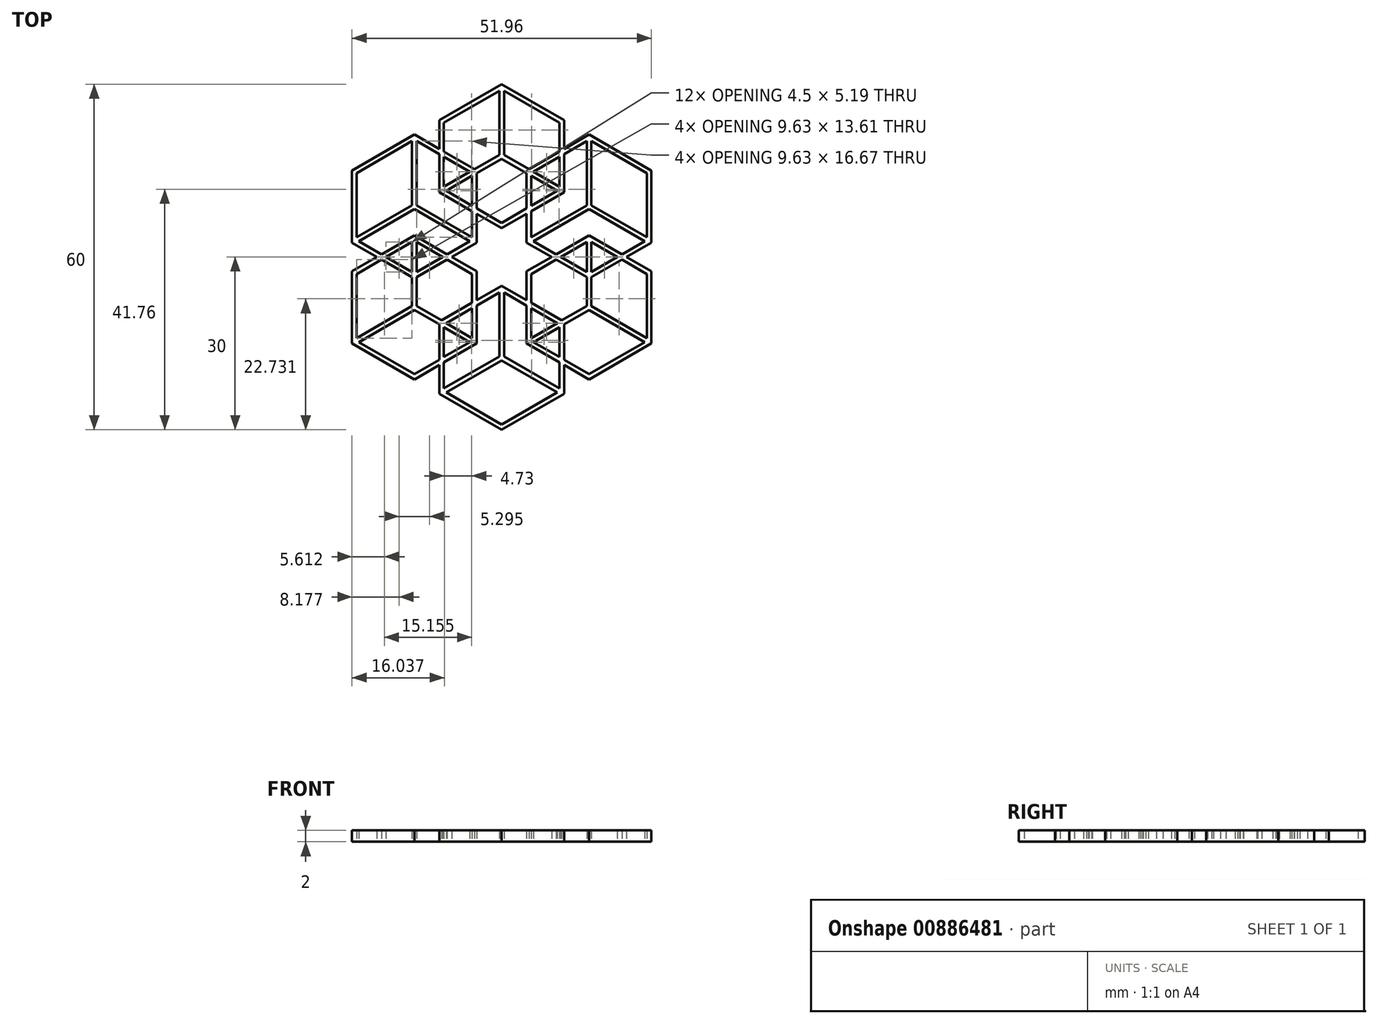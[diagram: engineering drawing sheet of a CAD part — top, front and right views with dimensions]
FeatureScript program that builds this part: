
annotation { "Feature Type Name" : "Feature", "Feature Type Description" : "" }
export const myFeature = defineFeature(function(context is Context, id is Id, definition is map)
    precondition{}
    {
        {
            var Q0;
            Q0=qCreatedBy(makeId("Top.planeOp"),FACE);
            var sketch = newSketch(context, id + "F0", { "sketchPlane" : qUnion([Q0])});
            skCircle(sketch, "E0.cCircle", {"center": v(0, 0) * mm, "radius": 30 * mm, "construction": true});
            skLineSegment(sketch, "E0.0", {"start": v(-25.98, 15) * mm, "end": v(0, 30) * mm, "construction": true});
            skLineSegment(sketch, "E0.1", {"start": v(0, 30) * mm, "end": v(25.98, 15) * mm, "construction": true});
            skLineSegment(sketch, "E0.2", {"start": v(25.98, 15) * mm, "end": v(25.98, -15) * mm, "construction": true});
            skLineSegment(sketch, "E0.3", {"start": v(25.98, -15) * mm, "end": v(0, -30) * mm, "construction": true});
            skLineSegment(sketch, "E0.4", {"start": v(0, -30) * mm, "end": v(-25.98, -15) * mm, "construction": true});
            skLineSegment(sketch, "E0.5", {"start": v(-25.98, -15) * mm, "end": v(-25.98, 15) * mm, "construction": true});
            skCircle(sketch, "E1.cCircle", {"center": v(0, -17.5) * mm, "radius": 12.5 * mm, "construction": true});
            skLineSegment(sketch, "E1.0", {"start": v(0, -30) * mm, "end": v(-10.83, -23.75) * mm});
            skLineSegment(sketch, "E1.1", {"start": v(-10.83, -23.75) * mm, "end": v(-10.83, -11.25) * mm});
            skLineSegment(sketch, "E1.2", {"start": v(-10.83, -11.25) * mm, "end": v(0, -5) * mm});
            skLineSegment(sketch, "E1.3", {"start": v(0, -5) * mm, "end": v(10.83, -11.25) * mm});
            skLineSegment(sketch, "E1.4", {"start": v(10.83, -11.25) * mm, "end": v(10.83, -23.75) * mm});
            skLineSegment(sketch, "E1.5", {"start": v(10.83, -23.75) * mm, "end": v(0, -30) * mm});
            skCircle(sketch, "E2.cCircle", {"center": v(0, -17.5) * mm, "radius": 11.58 * mm, "construction": true});
            skLineSegment(sketch, "E2.0", {"start": v(0.4, -6.15) * mm, "end": v(10.03, -11.71) * mm});
            skLineSegment(sketch, "E2.1", {"start": v(10.03, -11.71) * mm, "end": v(10.03, -22.83) * mm});
            skLineSegment(sketch, "E2.2", {"start": v(9.63, -23.52) * mm, "end": v(0, -29.08) * mm});
            skLineSegment(sketch, "E2.3", {"start": v(0, -29.08) * mm, "end": v(-9.63, -23.52) * mm});
            skLineSegment(sketch, "E2.4", {"start": v(-10.03, -22.83) * mm, "end": v(-10.03, -11.71) * mm});
            skLineSegment(sketch, "E2.5", {"start": v(-10.03, -11.71) * mm, "end": v(-0.4, -6.15) * mm});
            skLineSegment(sketch, "E3.0", {"start": v(0, -17.96) * mm, "end": v(9.63, -23.52) * mm});
            skLineSegment(sketch, "E4.0", {"start": v(0.4, -17.27) * mm, "end": v(10.03, -22.83) * mm});
            skLineSegment(sketch, "E5.0", {"start": v(-0.4, -17.27) * mm, "end": v(-10.03, -22.83) * mm});
            skLineSegment(sketch, "E6.0", {"start": v(0, -17.96) * mm, "end": v(-9.63, -23.52) * mm});
            skPoint(sketch, "E7.orphan", {"position": v(-10.03, -23.29) * mm});
            skLineSegment(sketch, "E8.trimOffspring", {"start": v(-0.4, -6.15) * mm, "end": v(-0.4, -17.27) * mm});
            skLineSegment(sketch, "E9.trimOffspring", {"start": v(0.4, -6.15) * mm, "end": v(0.4, -17.27) * mm});
            skPoint(sketch, "E10.orphan", {"position": v(0, -5.92) * mm});
            skLineSegment(sketch, "E11", {"start": v(0, -17.5) * mm, "end": v(10.83, -23.75) * mm, "construction": true});
            skLineSegment(sketch, "E12", {"start": v(0, -17.5) * mm, "end": v(-10.83, -23.75) * mm, "construction": true});
            skCircle(sketch, "E13.cCircle", {"center": v(15.16, -8.75) * mm, "radius": 12.5 * mm, "construction": true});
            skLineSegment(sketch, "E13.0", {"start": v(15.16, -21.25) * mm, "end": v(4.33, -15) * mm});
            skLineSegment(sketch, "E13.1", {"start": v(4.33, -15) * mm, "end": v(4.33, -2.5) * mm});
            skLineSegment(sketch, "E13.2", {"start": v(4.33, -2.5) * mm, "end": v(15.16, 3.75) * mm});
            skLineSegment(sketch, "E13.3", {"start": v(15.16, 3.75) * mm, "end": v(25.98, -2.5) * mm});
            skLineSegment(sketch, "E13.4", {"start": v(25.98, -2.5) * mm, "end": v(25.98, -15) * mm});
            skLineSegment(sketch, "E13.5", {"start": v(25.98, -15) * mm, "end": v(15.16, -21.25) * mm});
            skCircle(sketch, "E14.cCircle", {"center": v(15.16, -8.75) * mm, "radius": 11.58 * mm, "construction": true});
            skLineSegment(sketch, "E14.0", {"start": v(15.56, 2.6) * mm, "end": v(25.18, -2.96) * mm});
            skLineSegment(sketch, "E14.1", {"start": v(25.18, -2.96) * mm, "end": v(25.18, -14.08) * mm});
            skLineSegment(sketch, "E14.2", {"start": v(24.78, -14.77) * mm, "end": v(15.16, -20.33) * mm});
            skLineSegment(sketch, "E14.3", {"start": v(15.16, -20.33) * mm, "end": v(5.53, -14.77) * mm});
            skLineSegment(sketch, "E14.4", {"start": v(5.13, -14.08) * mm, "end": v(5.13, -2.96) * mm});
            skLineSegment(sketch, "E14.5", {"start": v(5.13, -2.96) * mm, "end": v(14.76, 2.6) * mm});
            skLineSegment(sketch, "E15.0", {"start": v(15.16, -9.21) * mm, "end": v(24.78, -14.77) * mm});
            skLineSegment(sketch, "E16.0", {"start": v(15.56, -8.52) * mm, "end": v(25.18, -14.08) * mm});
            skLineSegment(sketch, "E17.0", {"start": v(14.76, -8.52) * mm, "end": v(5.13, -14.08) * mm});
            skLineSegment(sketch, "E18.0", {"start": v(15.16, -9.21) * mm, "end": v(5.53, -14.77) * mm});
            skPoint(sketch, "E19.orphan", {"position": v(5.13, -14.54) * mm});
            skLineSegment(sketch, "E20.trimOffspring", {"start": v(14.76, 2.6) * mm, "end": v(14.76, -8.52) * mm});
            skLineSegment(sketch, "E21.trimOffspring", {"start": v(15.56, 2.6) * mm, "end": v(15.56, -8.52) * mm});
            skPoint(sketch, "E22.orphan", {"position": v(15.16, 2.83) * mm});
            skLineSegment(sketch, "E23", {"start": v(15.16, -8.75) * mm, "end": v(25.98, -15) * mm, "construction": true});
            skLineSegment(sketch, "E24", {"start": v(15.16, -8.75) * mm, "end": v(4.33, -15) * mm, "construction": true});
            skCircle(sketch, "E25.cCircle", {"center": v(-15.16, -8.75) * mm, "radius": 12.5 * mm, "construction": true});
            skLineSegment(sketch, "E25.0", {"start": v(-15.16, -21.25) * mm, "end": v(-25.98, -15) * mm});
            skLineSegment(sketch, "E25.1", {"start": v(-25.98, -15) * mm, "end": v(-25.98, -2.5) * mm});
            skLineSegment(sketch, "E25.2", {"start": v(-25.98, -2.5) * mm, "end": v(-15.16, 3.75) * mm});
            skLineSegment(sketch, "E25.3", {"start": v(-15.16, 3.75) * mm, "end": v(-4.33, -2.5) * mm});
            skLineSegment(sketch, "E25.4", {"start": v(-4.33, -2.5) * mm, "end": v(-4.33, -15) * mm});
            skLineSegment(sketch, "E25.5", {"start": v(-4.33, -15) * mm, "end": v(-15.16, -21.25) * mm});
            skCircle(sketch, "E26.cCircle", {"center": v(-15.16, -8.75) * mm, "radius": 11.58 * mm, "construction": true});
            skLineSegment(sketch, "E26.0", {"start": v(-14.76, 2.6) * mm, "end": v(-5.13, -2.96) * mm});
            skLineSegment(sketch, "E26.1", {"start": v(-5.13, -2.96) * mm, "end": v(-5.13, -14.08) * mm});
            skLineSegment(sketch, "E26.2", {"start": v(-5.53, -14.77) * mm, "end": v(-15.16, -20.33) * mm});
            skLineSegment(sketch, "E26.3", {"start": v(-15.16, -20.33) * mm, "end": v(-24.78, -14.77) * mm});
            skLineSegment(sketch, "E26.4", {"start": v(-25.18, -14.08) * mm, "end": v(-25.18, -2.96) * mm});
            skLineSegment(sketch, "E26.5", {"start": v(-25.18, -2.96) * mm, "end": v(-15.56, 2.6) * mm});
            skLineSegment(sketch, "E27.0", {"start": v(-15.16, -9.21) * mm, "end": v(-5.53, -14.77) * mm});
            skLineSegment(sketch, "E28.0", {"start": v(-14.76, -8.52) * mm, "end": v(-5.13, -14.08) * mm});
            skLineSegment(sketch, "E29.0", {"start": v(-15.56, -8.52) * mm, "end": v(-25.18, -14.08) * mm});
            skLineSegment(sketch, "E30.0", {"start": v(-15.16, -9.21) * mm, "end": v(-24.78, -14.77) * mm});
            skPoint(sketch, "E31.orphan", {"position": v(-25.18, -14.54) * mm});
            skLineSegment(sketch, "E32.trimOffspring", {"start": v(-15.56, 2.6) * mm, "end": v(-15.56, -8.52) * mm});
            skLineSegment(sketch, "E33.trimOffspring", {"start": v(-14.76, 2.6) * mm, "end": v(-14.76, -8.52) * mm});
            skPoint(sketch, "E34.orphan", {"position": v(-15.16, 2.83) * mm});
            skLineSegment(sketch, "E35", {"start": v(-15.16, -8.75) * mm, "end": v(-4.33, -15) * mm, "construction": true});
            skLineSegment(sketch, "E36", {"start": v(-15.16, -8.75) * mm, "end": v(-25.98, -15) * mm, "construction": true});
            skCircle(sketch, "E37.cCircle", {"center": v(0, 17.5) * mm, "radius": 12.5 * mm, "construction": true});
            skLineSegment(sketch, "E37.0", {"start": v(0, 5) * mm, "end": v(-10.83, 11.25) * mm});
            skLineSegment(sketch, "E37.1", {"start": v(-10.83, 11.25) * mm, "end": v(-10.83, 23.75) * mm});
            skLineSegment(sketch, "E37.2", {"start": v(-10.83, 23.75) * mm, "end": v(0, 30) * mm});
            skLineSegment(sketch, "E37.3", {"start": v(0, 30) * mm, "end": v(10.83, 23.75) * mm});
            skLineSegment(sketch, "E37.4", {"start": v(10.83, 23.75) * mm, "end": v(10.83, 11.25) * mm});
            skLineSegment(sketch, "E37.5", {"start": v(10.83, 11.25) * mm, "end": v(0, 5) * mm});
            skCircle(sketch, "E38.cCircle", {"center": v(0, 17.5) * mm, "radius": 11.58 * mm, "construction": true});
            skLineSegment(sketch, "E38.0", {"start": v(0.4, 28.85) * mm, "end": v(10.03, 23.29) * mm});
            skLineSegment(sketch, "E38.1", {"start": v(10.03, 23.29) * mm, "end": v(10.03, 12.17) * mm});
            skLineSegment(sketch, "E38.2", {"start": v(9.63, 11.48) * mm, "end": v(0, 5.92) * mm});
            skLineSegment(sketch, "E38.3", {"start": v(0, 5.92) * mm, "end": v(-9.63, 11.48) * mm});
            skLineSegment(sketch, "E38.4", {"start": v(-10.03, 12.17) * mm, "end": v(-10.03, 23.29) * mm});
            skLineSegment(sketch, "E38.5", {"start": v(-10.03, 23.29) * mm, "end": v(-0.4, 28.85) * mm});
            skLineSegment(sketch, "E39.0", {"start": v(0, 17.04) * mm, "end": v(9.63, 11.48) * mm});
            skLineSegment(sketch, "E40.0", {"start": v(0.4, 17.73) * mm, "end": v(10.03, 12.17) * mm});
            skLineSegment(sketch, "E41.0", {"start": v(-0.4, 17.73) * mm, "end": v(-10.03, 12.17) * mm});
            skLineSegment(sketch, "E42.0", {"start": v(0, 17.04) * mm, "end": v(-9.63, 11.48) * mm});
            skLineSegment(sketch, "E43.trimOffspring", {"start": v(-0.4, 28.85) * mm, "end": v(-0.4, 17.73) * mm});
            skLineSegment(sketch, "E44.trimOffspring", {"start": v(0.4, 28.85) * mm, "end": v(0.4, 17.73) * mm});
            skPoint(sketch, "E45.orphan", {"position": v(0, 29.08) * mm});
            skLineSegment(sketch, "E46", {"start": v(0, 17.5) * mm, "end": v(10.83, 11.25) * mm, "construction": true});
            skLineSegment(sketch, "E47", {"start": v(0, 17.5) * mm, "end": v(-10.83, 11.25) * mm, "construction": true});
            skCircle(sketch, "E48.cCircle", {"center": v(-15.16, 8.75) * mm, "radius": 12.5 * mm, "construction": true});
            skLineSegment(sketch, "E48.0", {"start": v(-15.16, -3.75) * mm, "end": v(-25.98, 2.5) * mm});
            skLineSegment(sketch, "E48.1", {"start": v(-25.98, 2.5) * mm, "end": v(-25.98, 15) * mm});
            skLineSegment(sketch, "E48.2", {"start": v(-25.98, 15) * mm, "end": v(-15.16, 21.25) * mm});
            skLineSegment(sketch, "E48.3", {"start": v(-15.16, 21.25) * mm, "end": v(-4.33, 15) * mm});
            skLineSegment(sketch, "E48.4", {"start": v(-4.33, 15) * mm, "end": v(-4.33, 2.5) * mm});
            skLineSegment(sketch, "E48.5", {"start": v(-4.33, 2.5) * mm, "end": v(-15.16, -3.75) * mm});
            skCircle(sketch, "E49.cCircle", {"center": v(-15.16, 8.75) * mm, "radius": 11.58 * mm, "construction": true});
            skLineSegment(sketch, "E49.0", {"start": v(-14.76, 20.1) * mm, "end": v(-5.13, 14.54) * mm});
            skLineSegment(sketch, "E49.1", {"start": v(-5.13, 14.54) * mm, "end": v(-5.13, 3.42) * mm});
            skLineSegment(sketch, "E49.2", {"start": v(-5.53, 2.73) * mm, "end": v(-15.16, -2.83) * mm});
            skLineSegment(sketch, "E49.3", {"start": v(-15.16, -2.83) * mm, "end": v(-24.78, 2.73) * mm});
            skLineSegment(sketch, "E49.4", {"start": v(-25.18, 3.42) * mm, "end": v(-25.18, 14.54) * mm});
            skLineSegment(sketch, "E49.5", {"start": v(-25.18, 14.54) * mm, "end": v(-15.56, 20.1) * mm});
            skLineSegment(sketch, "E50.0", {"start": v(-15.16, 8.29) * mm, "end": v(-5.53, 2.73) * mm});
            skLineSegment(sketch, "E51.0", {"start": v(-14.76, 8.98) * mm, "end": v(-5.13, 3.42) * mm});
            skLineSegment(sketch, "E52.0", {"start": v(-15.56, 8.98) * mm, "end": v(-25.18, 3.42) * mm});
            skLineSegment(sketch, "E53.0", {"start": v(-15.16, 8.29) * mm, "end": v(-24.78, 2.73) * mm});
            skPoint(sketch, "E54.orphan", {"position": v(-25.18, 2.96) * mm});
            skLineSegment(sketch, "E55.trimOffspring", {"start": v(-15.56, 20.1) * mm, "end": v(-15.56, 8.98) * mm});
            skLineSegment(sketch, "E56.trimOffspring", {"start": v(-14.76, 20.1) * mm, "end": v(-14.76, 8.98) * mm});
            skPoint(sketch, "E57.orphan", {"position": v(-15.16, 20.33) * mm});
            skLineSegment(sketch, "E58", {"start": v(-15.16, 8.75) * mm, "end": v(-4.33, 2.5) * mm, "construction": true});
            skLineSegment(sketch, "E59", {"start": v(-15.16, 8.75) * mm, "end": v(-25.98, 2.5) * mm, "construction": true});
            skCircle(sketch, "E60.cCircle", {"center": v(15.16, 8.75) * mm, "radius": 12.5 * mm, "construction": true});
            skLineSegment(sketch, "E60.0", {"start": v(15.16, -3.75) * mm, "end": v(4.33, 2.5) * mm});
            skLineSegment(sketch, "E60.1", {"start": v(4.33, 2.5) * mm, "end": v(4.33, 15) * mm});
            skLineSegment(sketch, "E60.2", {"start": v(4.33, 15) * mm, "end": v(15.16, 21.25) * mm});
            skLineSegment(sketch, "E60.3", {"start": v(15.16, 21.25) * mm, "end": v(25.98, 15) * mm});
            skLineSegment(sketch, "E60.4", {"start": v(25.98, 15) * mm, "end": v(25.98, 2.5) * mm});
            skLineSegment(sketch, "E60.5", {"start": v(25.98, 2.5) * mm, "end": v(15.16, -3.75) * mm});
            skCircle(sketch, "E61.cCircle", {"center": v(15.16, 8.75) * mm, "radius": 11.58 * mm, "construction": true});
            skLineSegment(sketch, "E61.0", {"start": v(15.56, 20.1) * mm, "end": v(25.18, 14.54) * mm});
            skLineSegment(sketch, "E61.1", {"start": v(25.18, 14.54) * mm, "end": v(25.18, 3.42) * mm});
            skLineSegment(sketch, "E61.2", {"start": v(24.78, 2.73) * mm, "end": v(15.16, -2.83) * mm});
            skLineSegment(sketch, "E61.3", {"start": v(15.16, -2.83) * mm, "end": v(5.53, 2.73) * mm});
            skLineSegment(sketch, "E61.4", {"start": v(5.13, 3.42) * mm, "end": v(5.13, 14.54) * mm});
            skLineSegment(sketch, "E61.5", {"start": v(5.13, 14.54) * mm, "end": v(14.76, 20.1) * mm});
            skLineSegment(sketch, "E62.0", {"start": v(15.16, 8.29) * mm, "end": v(24.78, 2.73) * mm});
            skLineSegment(sketch, "E63.0", {"start": v(15.56, 8.98) * mm, "end": v(25.18, 3.42) * mm});
            skLineSegment(sketch, "E64.0", {"start": v(14.76, 8.98) * mm, "end": v(5.13, 3.42) * mm});
            skLineSegment(sketch, "E65.0", {"start": v(15.16, 8.29) * mm, "end": v(5.53, 2.73) * mm});
            skLineSegment(sketch, "E66.trimOffspring", {"start": v(14.76, 20.1) * mm, "end": v(14.76, 8.98) * mm});
            skLineSegment(sketch, "E67.trimOffspring", {"start": v(15.56, 20.1) * mm, "end": v(15.56, 8.98) * mm});
            skPoint(sketch, "E68.orphan", {"position": v(15.16, 20.33) * mm});
            skLineSegment(sketch, "E69", {"start": v(15.16, 8.75) * mm, "end": v(25.98, 2.5) * mm, "construction": true});
            skLineSegment(sketch, "E70", {"start": v(15.16, 8.75) * mm, "end": v(4.33, 2.5) * mm, "construction": true});
            skSolve(sketch);
        }
        {
            var Q0;
            {var subQ5=sQuery(id+"F0.wireOp",EDGE,"E25.3");var subQ6=sQuery(id+"F0.wireOp",EDGE,"E25.2");var subQ7=makeQuery(id+"F0.imprint","INTERSECT",VERTEX,{"derivedFrom":[subQ6,subQ5]});Q0=makeQuery(id+"F0.imprint","IMPRINT",FACE,{"disambiguationData":[TD([[makeQuery(id+"F0.imprint","IMPRINT",EDGE,{"disambiguationData":[TD([[subQ7,1.0]])],"derivedFrom":subQ6}),-1.0]])]});}
            var Q1;
            {var subQ3=sQuery(id+"F0.wireOp",EDGE,"E25.0");Q1=makeQuery(id+"F0.imprint","IMPRINT",FACE,{"disambiguationData":[TD([[makeQuery(id+"F0.imprint","IMPRINT",EDGE,{"derivedFrom":subQ3}),-1.0]])]});}
            var Q2;
            {var subQ1=sQuery(id+"F0.wireOp",EDGE,"E2.4");var subQ11=sQuery(id+"F0.wireOp",EDGE,"E25.5");var subQ12=makeQuery(id+"F0.imprint","INTERSECT",VERTEX,{"derivedFrom":[subQ1,subQ11]});Q2=makeQuery(id+"F0.imprint","IMPRINT",FACE,{"disambiguationData":[TD([[makeQuery(id+"F0.imprint","IMPRINT",EDGE,{"disambiguationData":[TD([[subQ12,-1.0]])],"derivedFrom":subQ1}),-1.0]])]});}
            var Q3;
            {var subQ0=sQuery(id+"F0.wireOp",EDGE,"E26.1");var subQ9=sQuery(id+"F0.wireOp",EDGE,"E1.2");var subQ11=makeQuery(id+"F0.imprint","INTERSECT",VERTEX,{"derivedFrom":[subQ9,subQ0]});Q3=makeQuery(id+"F0.imprint","IMPRINT",FACE,{"disambiguationData":[TD([[makeQuery(id+"F0.imprint","IMPRINT",EDGE,{"disambiguationData":[TD([[subQ11,-1.0]])],"derivedFrom":subQ9}),1.0]])]});}
            var Q4;
            {var subQ0=sQuery(id+"F0.wireOp",EDGE,"E49.2");var subQ1=sQuery(id+"F0.wireOp",EDGE,"E26.0");var subQ2=makeQuery(id+"F0.imprint","INTERSECT",VERTEX,{"derivedFrom":[subQ1,subQ0]});Q4=makeQuery(id+"F0.imprint","IMPRINT",FACE,{"disambiguationData":[TD([[makeQuery(id+"F0.imprint","IMPRINT",EDGE,{"disambiguationData":[TD([[subQ2,-1.0]])],"derivedFrom":subQ1}),-1.0]])]});}
            var Q5;
            {var subQ0=sQuery(id+"F0.wireOp",EDGE,"E48.0");var subQ1=sQuery(id+"F0.wireOp",EDGE,"E26.5");var subQ2=makeQuery(id+"F0.imprint","INTERSECT",VERTEX,{"derivedFrom":[subQ1,subQ0]});Q5=makeQuery(id+"F0.imprint","IMPRINT",FACE,{"disambiguationData":[TD([[makeQuery(id+"F0.imprint","IMPRINT",EDGE,{"disambiguationData":[TD([[subQ2,-1.0]])],"derivedFrom":subQ1}),-1.0]])]});}
            var Q6;
            {var subQ5=sQuery(id+"F0.wireOp",EDGE,"E32.trimOffspring");var subQ9=sQuery(id+"F0.wireOp",EDGE,"E49.3");var subQ10=makeQuery(id+"F0.imprint","INTERSECT",VERTEX,{"derivedFrom":[subQ5,subQ9]});Q6=makeQuery(id+"F0.imprint","IMPRINT",FACE,{"disambiguationData":[TD([[makeQuery(id+"F0.imprint","IMPRINT",EDGE,{"disambiguationData":[TD([[subQ10,-1.0]])],"derivedFrom":subQ5}),1.0]])]});}
            var Q7;
            {var subQ0=sQuery(id+"F0.wireOp",EDGE,"E48.0");var subQ1=sQuery(id+"F0.wireOp",EDGE,"E25.2");var subQ2=makeQuery(id+"F0.imprint","INTERSECT",VERTEX,{"derivedFrom":[subQ1,subQ0]});Q7=makeQuery(id+"F0.imprint","IMPRINT",FACE,{"disambiguationData":[TD([[makeQuery(id+"F0.imprint","IMPRINT",EDGE,{"disambiguationData":[TD([[subQ2,-1.0]])],"derivedFrom":subQ1}),-1.0]])]});}
            var Q8;
            {var subQ0=sQuery(id+"F0.wireOp",EDGE,"E49.2");var subQ1=sQuery(id+"F0.wireOp",EDGE,"E25.3");var subQ2=makeQuery(id+"F0.imprint","INTERSECT",VERTEX,{"derivedFrom":[subQ1,subQ0]});Q8=makeQuery(id+"F0.imprint","IMPRINT",FACE,{"disambiguationData":[TD([[makeQuery(id+"F0.imprint","IMPRINT",EDGE,{"disambiguationData":[TD([[subQ2,-1.0]])],"derivedFrom":subQ1}),-1.0]])]});}
            var Q9;
            {var subQ9=sQuery(id+"F0.wireOp",EDGE,"E48.1");Q9=makeQuery(id+"F0.imprint","IMPRINT",FACE,{"disambiguationData":[TD([[makeQuery(id+"F0.imprint","IMPRINT",EDGE,{"derivedFrom":subQ9}),-1.0]])]});}
            var Q10;
            {var subQ0=sQuery(id+"F0.wireOp",EDGE,"E28.0");var subQ1=sQuery(id+"F0.wireOp",EDGE,"E1.2");var subQ2=makeQuery(id+"F0.imprint","INTERSECT",VERTEX,{"derivedFrom":[subQ1,subQ0]});Q10=makeQuery(id+"F0.imprint","IMPRINT",FACE,{"disambiguationData":[TD([[makeQuery(id+"F0.imprint","IMPRINT",EDGE,{"disambiguationData":[TD([[subQ2,-1.0]])],"derivedFrom":subQ1}),-1.0]])]});}
            var Q11;
            {var subQ0=sQuery(id+"F0.wireOp",EDGE,"E26.1");var subQ1=sQuery(id+"F0.wireOp",EDGE,"E1.2");var subQ2=makeQuery(id+"F0.imprint","INTERSECT",VERTEX,{"derivedFrom":[subQ1,subQ0]});Q11=makeQuery(id+"F0.imprint","IMPRINT",FACE,{"disambiguationData":[TD([[makeQuery(id+"F0.imprint","IMPRINT",EDGE,{"disambiguationData":[TD([[subQ2,-1.0]])],"derivedFrom":subQ1}),-1.0]])]});}
            var Q12;
            {var subQ0=sQuery(id+"F0.wireOp",EDGE,"E26.2");var subQ1=sQuery(id+"F0.wireOp",EDGE,"E1.1");var subQ2=makeQuery(id+"F0.imprint","INTERSECT",VERTEX,{"derivedFrom":[subQ1,subQ0]});Q12=makeQuery(id+"F0.imprint","IMPRINT",FACE,{"disambiguationData":[TD([[makeQuery(id+"F0.imprint","IMPRINT",EDGE,{"disambiguationData":[TD([[subQ2,-1.0]])],"derivedFrom":subQ1}),-1.0]])]});}
            var Q13;
            {var subQ7=sQuery(id+"F0.wireOp",EDGE,"E1.2");var subQ8=sQuery(id+"F0.wireOp",EDGE,"E1.1");var subQ9=makeQuery(id+"F0.imprint","INTERSECT",VERTEX,{"derivedFrom":[subQ8,subQ7]});Q13=makeQuery(id+"F0.imprint","IMPRINT",FACE,{"disambiguationData":[TD([[makeQuery(id+"F0.imprint","IMPRINT",EDGE,{"disambiguationData":[TD([[subQ9,1.0]])],"derivedFrom":subQ8}),-1.0]])]});}
            var Q14;
            {var subQ17=sQuery(id+"F0.wireOp",EDGE,"E1.0");Q14=makeQuery(id+"F0.imprint","IMPRINT",FACE,{"disambiguationData":[TD([[makeQuery(id+"F0.imprint","IMPRINT",EDGE,{"derivedFrom":subQ17}),-1.0]])]});}
            var Q15;
            {var subQ0=sQuery(id+"F0.wireOp",EDGE,"E25.5");var subQ1=sQuery(id+"F0.wireOp",EDGE,"E1.1");var subQ2=makeQuery(id+"F0.imprint","INTERSECT",VERTEX,{"derivedFrom":[subQ1,subQ0]});Q15=makeQuery(id+"F0.imprint","IMPRINT",FACE,{"disambiguationData":[TD([[makeQuery(id+"F0.imprint","IMPRINT",EDGE,{"disambiguationData":[TD([[subQ2,-1.0]])],"derivedFrom":subQ1}),-1.0]])]});}
            var Q16;
            {var subQ5=sQuery(id+"F0.wireOp",EDGE,"E37.1");var subQ6=sQuery(id+"F0.wireOp",EDGE,"E37.0");var subQ7=makeQuery(id+"F0.imprint","INTERSECT",VERTEX,{"derivedFrom":[subQ6,subQ5]});Q16=makeQuery(id+"F0.imprint","IMPRINT",FACE,{"disambiguationData":[TD([[makeQuery(id+"F0.imprint","IMPRINT",EDGE,{"disambiguationData":[TD([[subQ7,1.0]])],"derivedFrom":subQ6}),-1.0]])]});}
            var Q17;
            {var subQ0=sQuery(id+"F0.wireOp",EDGE,"E48.4");var subQ1=sQuery(id+"F0.wireOp",EDGE,"E37.0");var subQ2=makeQuery(id+"F0.imprint","INTERSECT",VERTEX,{"derivedFrom":[subQ1,subQ0]});Q17=makeQuery(id+"F0.imprint","IMPRINT",FACE,{"disambiguationData":[TD([[makeQuery(id+"F0.imprint","IMPRINT",EDGE,{"disambiguationData":[TD([[subQ2,-1.0]])],"derivedFrom":subQ1}),-1.0]])]});}
            var Q18;
            {var subQ0=sQuery(id+"F0.wireOp",EDGE,"E48.4");var subQ1=sQuery(id+"F0.wireOp",EDGE,"E38.3");var subQ2=makeQuery(id+"F0.imprint","INTERSECT",VERTEX,{"derivedFrom":[subQ1,subQ0]});Q18=makeQuery(id+"F0.imprint","IMPRINT",FACE,{"disambiguationData":[TD([[makeQuery(id+"F0.imprint","IMPRINT",EDGE,{"disambiguationData":[TD([[subQ2,-1.0]])],"derivedFrom":subQ1}),-1.0]])]});}
            var Q19;
            {var subQ0=sQuery(id+"F0.wireOp",EDGE,"E49.0");var subQ1=sQuery(id+"F0.wireOp",EDGE,"E38.4");var subQ2=makeQuery(id+"F0.imprint","INTERSECT",VERTEX,{"derivedFrom":[subQ1,subQ0]});Q19=makeQuery(id+"F0.imprint","IMPRINT",FACE,{"disambiguationData":[TD([[makeQuery(id+"F0.imprint","IMPRINT",EDGE,{"disambiguationData":[TD([[subQ2,-1.0]])],"derivedFrom":subQ1}),-1.0]])]});}
            var Q20;
            {var subQ0=sQuery(id+"F0.wireOp",EDGE,"E48.3");var subQ1=sQuery(id+"F0.wireOp",EDGE,"E37.1");var subQ2=makeQuery(id+"F0.imprint","INTERSECT",VERTEX,{"derivedFrom":[subQ1,subQ0]});Q20=makeQuery(id+"F0.imprint","IMPRINT",FACE,{"disambiguationData":[TD([[makeQuery(id+"F0.imprint","IMPRINT",EDGE,{"disambiguationData":[TD([[subQ2,1.0]])],"derivedFrom":subQ1}),-1.0]])]});}
            var Q21;
            {var subQ1=sQuery(id+"F0.wireOp",EDGE,"E48.3");var subQ8=sQuery(id+"F0.wireOp",EDGE,"E41.0");var subQ10=makeQuery(id+"F0.imprint","INTERSECT",VERTEX,{"derivedFrom":[subQ8,subQ1]});Q21=makeQuery(id+"F0.imprint","IMPRINT",FACE,{"disambiguationData":[TD([[makeQuery(id+"F0.imprint","IMPRINT",EDGE,{"disambiguationData":[TD([[subQ10,-1.0]])],"derivedFrom":subQ8}),1.0]])]});}
            var Q22;
            {var subQ21=sQuery(id+"F0.wireOp",EDGE,"E37.2");Q22=makeQuery(id+"F0.imprint","IMPRINT",FACE,{"disambiguationData":[TD([[makeQuery(id+"F0.imprint","IMPRINT",EDGE,{"derivedFrom":subQ21}),-1.0]])]});}
            var Q23;
            {var subQ5=sQuery(id+"F0.wireOp",EDGE,"E37.0");var subQ7=sQuery(id+"F0.wireOp",EDGE,"E37.5");var subQ8=makeQuery(id+"F0.imprint","INTERSECT",VERTEX,{"derivedFrom":[subQ5,subQ7]});Q23=makeQuery(id+"F0.imprint","IMPRINT",FACE,{"disambiguationData":[TD([[makeQuery(id+"F0.imprint","IMPRINT",EDGE,{"disambiguationData":[TD([[subQ8,-1.0]])],"derivedFrom":subQ5}),-1.0]])]});}
            var Q24;
            {var subQ0=sQuery(id+"F0.wireOp",EDGE,"E61.4");var subQ1=sQuery(id+"F0.wireOp",EDGE,"E37.5");var subQ2=makeQuery(id+"F0.imprint","INTERSECT",VERTEX,{"derivedFrom":[subQ1,subQ0]});Q24=makeQuery(id+"F0.imprint","IMPRINT",FACE,{"disambiguationData":[TD([[makeQuery(id+"F0.imprint","IMPRINT",EDGE,{"disambiguationData":[TD([[subQ2,-1.0]])],"derivedFrom":subQ1}),-1.0]])]});}
            var Q25;
            {var subQ0=sQuery(id+"F0.wireOp",EDGE,"E61.4");var subQ1=sQuery(id+"F0.wireOp",EDGE,"E38.2");var subQ2=makeQuery(id+"F0.imprint","INTERSECT",VERTEX,{"derivedFrom":[subQ1,subQ0]});Q25=makeQuery(id+"F0.imprint","IMPRINT",FACE,{"disambiguationData":[TD([[makeQuery(id+"F0.imprint","IMPRINT",EDGE,{"disambiguationData":[TD([[subQ2,-1.0]])],"derivedFrom":subQ1}),-1.0]])]});}
            var Q26;
            {var subQ12=sQuery(id+"F0.wireOp",EDGE,"E37.5");var subQ13=sQuery(id+"F0.wireOp",EDGE,"E37.4");var subQ14=makeQuery(id+"F0.imprint","INTERSECT",VERTEX,{"derivedFrom":[subQ13,subQ12]});Q26=makeQuery(id+"F0.imprint","IMPRINT",FACE,{"disambiguationData":[TD([[makeQuery(id+"F0.imprint","IMPRINT",EDGE,{"disambiguationData":[TD([[subQ14,1.0]])],"derivedFrom":subQ13}),-1.0]])]});}
            var Q27;
            {var subQ1=sQuery(id+"F0.wireOp",EDGE,"E60.1");var subQ3=sQuery(id+"F0.wireOp",EDGE,"E39.0");var subQ4=makeQuery(id+"F0.imprint","INTERSECT",VERTEX,{"derivedFrom":[subQ3,subQ1]});Q27=makeQuery(id+"F0.imprint","IMPRINT",FACE,{"disambiguationData":[TD([[makeQuery(id+"F0.imprint","IMPRINT",EDGE,{"disambiguationData":[TD([[subQ4,-1.0]])],"derivedFrom":subQ3}),1.0]])]});}
            var Q28;
            {var subQ0=sQuery(id+"F0.wireOp",EDGE,"E60.2");var subQ1=sQuery(id+"F0.wireOp",EDGE,"E38.1");var subQ2=makeQuery(id+"F0.imprint","INTERSECT",VERTEX,{"derivedFrom":[subQ1,subQ0]});Q28=makeQuery(id+"F0.imprint","IMPRINT",FACE,{"disambiguationData":[TD([[makeQuery(id+"F0.imprint","IMPRINT",EDGE,{"disambiguationData":[TD([[subQ2,-1.0]])],"derivedFrom":subQ1}),-1.0]])]});}
            var Q29;
            {var subQ0=sQuery(id+"F0.wireOp",EDGE,"E60.3");Q29=makeQuery(id+"F0.imprint","IMPRINT",FACE,{"disambiguationData":[TD([[makeQuery(id+"F0.imprint","IMPRINT",EDGE,{"derivedFrom":subQ0}),-1.0]])]});}
            var Q30;
            {var subQ0=sQuery(id+"F0.wireOp",EDGE,"E60.2");var subQ1=sQuery(id+"F0.wireOp",EDGE,"E37.4");var subQ2=makeQuery(id+"F0.imprint","INTERSECT",VERTEX,{"derivedFrom":[subQ1,subQ0]});Q30=makeQuery(id+"F0.imprint","IMPRINT",FACE,{"disambiguationData":[TD([[makeQuery(id+"F0.imprint","IMPRINT",EDGE,{"disambiguationData":[TD([[subQ2,-1.0]])],"derivedFrom":subQ1}),-1.0]])]});}
            var Q31;
            {var subQ0=sQuery(id+"F0.wireOp",EDGE,"E60.0");var subQ1=sQuery(id+"F0.wireOp",EDGE,"E14.5");var subQ2=makeQuery(id+"F0.imprint","INTERSECT",VERTEX,{"derivedFrom":[subQ1,subQ0]});Q31=makeQuery(id+"F0.imprint","IMPRINT",FACE,{"disambiguationData":[TD([[makeQuery(id+"F0.imprint","IMPRINT",EDGE,{"disambiguationData":[TD([[subQ2,-1.0]])],"derivedFrom":subQ1}),-1.0]])]});}
            var Q32;
            {var subQ0=sQuery(id+"F0.wireOp",EDGE,"E60.0");var subQ1=sQuery(id+"F0.wireOp",EDGE,"E13.2");var subQ2=makeQuery(id+"F0.imprint","INTERSECT",VERTEX,{"derivedFrom":[subQ1,subQ0]});Q32=makeQuery(id+"F0.imprint","IMPRINT",FACE,{"disambiguationData":[TD([[makeQuery(id+"F0.imprint","IMPRINT",EDGE,{"disambiguationData":[TD([[subQ2,-1.0]])],"derivedFrom":subQ1}),-1.0]])]});}
            var Q33;
            {var subQ12=sQuery(id+"F0.wireOp",EDGE,"E13.3");var subQ13=sQuery(id+"F0.wireOp",EDGE,"E13.2");var subQ14=makeQuery(id+"F0.imprint","INTERSECT",VERTEX,{"derivedFrom":[subQ13,subQ12]});Q33=makeQuery(id+"F0.imprint","IMPRINT",FACE,{"disambiguationData":[TD([[makeQuery(id+"F0.imprint","IMPRINT",EDGE,{"disambiguationData":[TD([[subQ14,1.0]])],"derivedFrom":subQ13}),-1.0]])]});}
            var Q34;
            {var subQ3=sQuery(id+"F0.wireOp",EDGE,"E20.trimOffspring");var subQ9=sQuery(id+"F0.wireOp",EDGE,"E61.3");var subQ10=makeQuery(id+"F0.imprint","INTERSECT",VERTEX,{"derivedFrom":[subQ3,subQ9]});Q34=makeQuery(id+"F0.imprint","IMPRINT",FACE,{"disambiguationData":[TD([[makeQuery(id+"F0.imprint","IMPRINT",EDGE,{"disambiguationData":[TD([[subQ10,-1.0]])],"derivedFrom":subQ3}),1.0]])]});}
            var Q35;
            {var subQ0=sQuery(id+"F0.wireOp",EDGE,"E61.2");var subQ1=sQuery(id+"F0.wireOp",EDGE,"E14.0");var subQ2=makeQuery(id+"F0.imprint","INTERSECT",VERTEX,{"derivedFrom":[subQ1,subQ0]});Q35=makeQuery(id+"F0.imprint","IMPRINT",FACE,{"disambiguationData":[TD([[makeQuery(id+"F0.imprint","IMPRINT",EDGE,{"disambiguationData":[TD([[subQ2,-1.0]])],"derivedFrom":subQ1}),-1.0]])]});}
            var Q36;
            {var subQ0=sQuery(id+"F0.wireOp",EDGE,"E60.5");var subQ1=sQuery(id+"F0.wireOp",EDGE,"E13.3");var subQ2=makeQuery(id+"F0.imprint","INTERSECT",VERTEX,{"derivedFrom":[subQ1,subQ0]});Q36=makeQuery(id+"F0.imprint","IMPRINT",FACE,{"disambiguationData":[TD([[makeQuery(id+"F0.imprint","IMPRINT",EDGE,{"disambiguationData":[TD([[subQ2,1.0]])],"derivedFrom":subQ1}),-1.0]])]});}
            var Q37;
            {var subQ14=sQuery(id+"F0.wireOp",EDGE,"E13.4");Q37=makeQuery(id+"F0.imprint","IMPRINT",FACE,{"disambiguationData":[TD([[makeQuery(id+"F0.imprint","IMPRINT",EDGE,{"derivedFrom":subQ14}),-1.0]])]});}
            var Q38;
            {var subQ3=sQuery(id+"F0.wireOp",EDGE,"E1.3");var subQ6=sQuery(id+"F0.wireOp",EDGE,"E13.1");var subQ10=makeQuery(id+"F0.imprint","INTERSECT",VERTEX,{"derivedFrom":[subQ3,subQ6]});Q38=makeQuery(id+"F0.imprint","IMPRINT",FACE,{"disambiguationData":[TD([[makeQuery(id+"F0.imprint","IMPRINT",EDGE,{"disambiguationData":[TD([[subQ10,-1.0]])],"derivedFrom":subQ3}),1.0]])]});}
            var Q39;
            {var subQ0=sQuery(id+"F0.wireOp",EDGE,"E13.1");var subQ1=sQuery(id+"F0.wireOp",EDGE,"E1.3");var subQ2=makeQuery(id+"F0.imprint","INTERSECT",VERTEX,{"derivedFrom":[subQ1,subQ0]});Q39=makeQuery(id+"F0.imprint","IMPRINT",FACE,{"disambiguationData":[TD([[makeQuery(id+"F0.imprint","IMPRINT",EDGE,{"disambiguationData":[TD([[subQ2,-1.0]])],"derivedFrom":subQ1}),-1.0]])]});}
            var Q40;
            {var subQ0=sQuery(id+"F0.wireOp",EDGE,"E14.4");var subQ1=sQuery(id+"F0.wireOp",EDGE,"E1.3");var subQ2=makeQuery(id+"F0.imprint","INTERSECT",VERTEX,{"derivedFrom":[subQ1,subQ0]});Q40=makeQuery(id+"F0.imprint","IMPRINT",FACE,{"disambiguationData":[TD([[makeQuery(id+"F0.imprint","IMPRINT",EDGE,{"disambiguationData":[TD([[subQ2,-1.0]])],"derivedFrom":subQ1}),-1.0]])]});}
            var Q41;
            {var subQ1=sQuery(id+"F0.wireOp",EDGE,"E2.0");var subQ5=sQuery(id+"F0.wireOp",EDGE,"E13.1");var subQ14=makeQuery(id+"F0.imprint","INTERSECT",VERTEX,{"derivedFrom":[subQ1,subQ5]});Q41=makeQuery(id+"F0.imprint","IMPRINT",FACE,{"disambiguationData":[TD([[makeQuery(id+"F0.imprint","IMPRINT",EDGE,{"disambiguationData":[TD([[subQ14,-1.0]])],"derivedFrom":subQ1}),-1.0]])]});}
            var Q42;
            {var subQ0=sQuery(id+"F0.wireOp",EDGE,"E18.0");var subQ1=sQuery(id+"F0.wireOp",EDGE,"E1.4");var subQ2=makeQuery(id+"F0.imprint","INTERSECT",VERTEX,{"derivedFrom":[subQ1,subQ0]});Q42=makeQuery(id+"F0.imprint","IMPRINT",FACE,{"disambiguationData":[TD([[makeQuery(id+"F0.imprint","IMPRINT",EDGE,{"disambiguationData":[TD([[subQ2,-1.0]])],"derivedFrom":subQ1}),-1.0]])]});}
            var Q43;
            {var subQ0=sQuery(id+"F0.wireOp",EDGE,"E13.0");var subQ1=sQuery(id+"F0.wireOp",EDGE,"E1.4");var subQ2=makeQuery(id+"F0.imprint","INTERSECT",VERTEX,{"derivedFrom":[subQ1,subQ0]});Q43=makeQuery(id+"F0.imprint","IMPRINT",FACE,{"disambiguationData":[TD([[makeQuery(id+"F0.imprint","IMPRINT",EDGE,{"disambiguationData":[TD([[subQ2,1.0]])],"derivedFrom":subQ1}),-1.0]])]});}
            var Q44;
            {var subQ6=sQuery(id+"F0.wireOp",EDGE,"E1.4");var subQ9=sQuery(id+"F0.wireOp",EDGE,"E1.3");var subQ10=makeQuery(id+"F0.imprint","INTERSECT",VERTEX,{"derivedFrom":[subQ9,subQ6]});Q44=makeQuery(id+"F0.imprint","IMPRINT",FACE,{"disambiguationData":[TD([[makeQuery(id+"F0.imprint","IMPRINT",EDGE,{"disambiguationData":[TD([[subQ10,1.0]])],"derivedFrom":subQ9}),-1.0]])]});}
            var Q45;
            {var subQ3=sQuery(id+"F0.wireOp",EDGE,"E2.1");var subQ7=sQuery(id+"F0.wireOp",EDGE,"E2.0");var subQ8=makeQuery(id+"F0.imprint","INTERSECT",VERTEX,{"derivedFrom":[subQ7,subQ3]});Q45=makeQuery(id+"F0.imprint","IMPRINT",FACE,{"disambiguationData":[TD([[makeQuery(id+"F0.imprint","IMPRINT",EDGE,{"disambiguationData":[TD([[subQ8,1.0]])],"derivedFrom":subQ7}),-1.0]])]});}
            var Q46;
            {var subQ0=sQuery(id+"F0.wireOp",EDGE,"0c9a6bff-b2c0-4d4d-a447-967ebe58276c.5");var subQ1=sQuery(id+"F0.wireOp",EDGE,"E1.3");var subQ2=makeQuery(id+"F0.imprint","INTERSECT",VERTEX,{"derivedFrom":[subQ1,subQ0]});Q46=makeQuery(id+"F0.imprint","IMPRINT",FACE,{"disambiguationData":[TD([[makeQuery(id+"F0.imprint","IMPRINT",EDGE,{"disambiguationData":[TD([[subQ2,-1.0]])],"derivedFrom":subQ1}),-1.0]])]});}
            var Q47;
            {var subQ5=sQuery(id+"F0.wireOp",EDGE,"E1.3");var subQ6=sQuery(id+"F0.wireOp",EDGE,"E1.2");var subQ7=makeQuery(id+"F0.imprint","INTERSECT",VERTEX,{"derivedFrom":[subQ6,subQ5]});Q47=makeQuery(id+"F0.imprint","IMPRINT",FACE,{"disambiguationData":[TD([[makeQuery(id+"F0.imprint","IMPRINT",EDGE,{"disambiguationData":[TD([[subQ7,1.0]])],"derivedFrom":subQ6}),-1.0]])]});}
            var Q48;
            {var subQ5=sQuery(id+"F0.wireOp",EDGE,"E2.0");var subQ7=sQuery(id+"F0.wireOp",EDGE,"fe7c7291-770d-4a74-9fde-94e01091e8e7.2");var subQ9=makeQuery(id+"F0.imprint","INTERSECT",VERTEX,{"derivedFrom":[subQ5,subQ7]});Q48=makeQuery(id+"F0.imprint","IMPRINT",FACE,{"disambiguationData":[TD([[makeQuery(id+"F0.imprint","IMPRINT",EDGE,{"disambiguationData":[TD([[subQ9,-1.0]])],"derivedFrom":subQ5}),-1.0]])]});}
            var Q49;
            {var subQ1=sQuery(id+"F0.wireOp",EDGE,"E1.3");var subQ7=sQuery(id+"F0.wireOp",EDGE,"fe7c7291-770d-4a74-9fde-94e01091e8e7.2");var subQ8=makeQuery(id+"F0.imprint","INTERSECT",VERTEX,{"derivedFrom":[subQ1,subQ7]});Q49=makeQuery(id+"F0.imprint","IMPRINT",FACE,{"disambiguationData":[TD([[makeQuery(id+"F0.imprint","IMPRINT",EDGE,{"disambiguationData":[TD([[subQ8,-1.0]])],"derivedFrom":subQ1}),-1.0]])]});}
            var Q50;
            {var subQ0=sQuery(id+"F0.wireOp",EDGE,"fe7c7291-770d-4a74-9fde-94e01091e8e7.2");var subQ1=sQuery(id+"F0.wireOp",EDGE,"E2.0");var subQ2=makeQuery(id+"F0.imprint","INTERSECT",VERTEX,{"derivedFrom":[subQ1,subQ0]});Q50=makeQuery(id+"F0.imprint","IMPRINT",FACE,{"disambiguationData":[TD([[makeQuery(id+"F0.imprint","IMPRINT",EDGE,{"disambiguationData":[TD([[subQ2,-1.0]])],"derivedFrom":subQ1}),1.0]])]});}
            var Q51;
            {var subQ5=sQuery(id+"F0.wireOp",EDGE,"E13.2");var subQ6=sQuery(id+"F0.wireOp",EDGE,"E13.1");var subQ7=makeQuery(id+"F0.imprint","INTERSECT",VERTEX,{"derivedFrom":[subQ6,subQ5]});Q51=makeQuery(id+"F0.imprint","IMPRINT",FACE,{"disambiguationData":[TD([[makeQuery(id+"F0.imprint","IMPRINT",EDGE,{"disambiguationData":[TD([[subQ7,1.0]])],"derivedFrom":subQ6}),-1.0]])]});}
            var Q52;
            {var subQ0=sQuery(id+"F0.wireOp",EDGE,"5f94be97-0224-4d17-be68-8b44869080e5.0");var subQ1=sQuery(id+"F0.wireOp",EDGE,"E13.2");var subQ2=makeQuery(id+"F0.imprint","INTERSECT",VERTEX,{"derivedFrom":[subQ1,subQ0]});Q52=makeQuery(id+"F0.imprint","IMPRINT",FACE,{"disambiguationData":[TD([[makeQuery(id+"F0.imprint","IMPRINT",EDGE,{"disambiguationData":[TD([[subQ2,-1.0]])],"derivedFrom":subQ1}),-1.0]])]});}
            var Q53;
            {var subQ7=sQuery(id+"F0.wireOp",EDGE,"E8.trimOffspring");var subQ9=sQuery(id+"F0.wireOp",EDGE,"fe7c7291-770d-4a74-9fde-94e01091e8e7.3");var subQ10=makeQuery(id+"F0.imprint","INTERSECT",VERTEX,{"derivedFrom":[subQ7,subQ9]});Q53=makeQuery(id+"F0.imprint","IMPRINT",FACE,{"disambiguationData":[TD([[makeQuery(id+"F0.imprint","IMPRINT",EDGE,{"disambiguationData":[TD([[subQ10,-1.0]])],"derivedFrom":subQ7}),1.0]])]});}
            var Q54;
            {var subQ0=sQuery(id+"F0.wireOp",EDGE,"E26.1");var subQ1=sQuery(id+"F0.wireOp",EDGE,"E2.5");var subQ2=makeQuery(id+"F0.imprint","INTERSECT",VERTEX,{"derivedFrom":[subQ1,subQ0]});Q54=makeQuery(id+"F0.imprint","IMPRINT",FACE,{"disambiguationData":[TD([[makeQuery(id+"F0.imprint","IMPRINT",EDGE,{"disambiguationData":[TD([[subQ2,-1.0]])],"derivedFrom":subQ1}),-1.0]])]});}
            var Q55;
            {var subQ0=sQuery(id+"F0.wireOp",EDGE,"fe7c7291-770d-4a74-9fde-94e01091e8e7.3");var subQ1=sQuery(id+"F0.wireOp",EDGE,"E2.5");var subQ2=makeQuery(id+"F0.imprint","INTERSECT",VERTEX,{"derivedFrom":[subQ1,subQ0]});Q55=makeQuery(id+"F0.imprint","IMPRINT",FACE,{"disambiguationData":[TD([[makeQuery(id+"F0.imprint","IMPRINT",EDGE,{"disambiguationData":[TD([[subQ2,-1.0]])],"derivedFrom":subQ1}),-1.0]])]});}
            var Q56;
            {var subQ0=sQuery(id+"F0.wireOp",EDGE,"E26.1");var subQ1=sQuery(id+"F0.wireOp",EDGE,"E2.5");var subQ2=makeQuery(id+"F0.imprint","INTERSECT",VERTEX,{"derivedFrom":[subQ1,subQ0]});Q56=makeQuery(id+"F0.imprint","IMPRINT",FACE,{"disambiguationData":[TD([[makeQuery(id+"F0.imprint","IMPRINT",EDGE,{"disambiguationData":[TD([[subQ2,-1.0]])],"derivedFrom":subQ1}),1.0]])]});}
            var Q57;
            {var subQ0=sQuery(id+"F0.wireOp",EDGE,"0c9a6bff-b2c0-4d4d-a447-967ebe58276c.0");var subQ1=sQuery(id+"F0.wireOp",EDGE,"E2.5");var subQ2=makeQuery(id+"F0.imprint","INTERSECT",VERTEX,{"derivedFrom":[subQ1,subQ0]});Q57=makeQuery(id+"F0.imprint","IMPRINT",FACE,{"disambiguationData":[TD([[makeQuery(id+"F0.imprint","IMPRINT",EDGE,{"disambiguationData":[TD([[subQ2,-1.0]])],"derivedFrom":subQ1}),-1.0]])]});}
            var Q58;
            {var subQ0=sQuery(id+"F0.wireOp",EDGE,"0c9a6bff-b2c0-4d4d-a447-967ebe58276c.0");var subQ1=sQuery(id+"F0.wireOp",EDGE,"E1.2");var subQ2=makeQuery(id+"F0.imprint","INTERSECT",VERTEX,{"derivedFrom":[subQ1,subQ0]});Q58=makeQuery(id+"F0.imprint","IMPRINT",FACE,{"disambiguationData":[TD([[makeQuery(id+"F0.imprint","IMPRINT",EDGE,{"disambiguationData":[TD([[subQ2,-1.0]])],"derivedFrom":subQ1}),-1.0]])]});}
            var Q59;
            {var subQ0=sQuery(id+"F0.wireOp",EDGE,"fe7c7291-770d-4a74-9fde-94e01091e8e7.3");var subQ1=sQuery(id+"F0.wireOp",EDGE,"E1.2");var subQ2=makeQuery(id+"F0.imprint","INTERSECT",VERTEX,{"derivedFrom":[subQ1,subQ0]});Q59=makeQuery(id+"F0.imprint","IMPRINT",FACE,{"disambiguationData":[TD([[makeQuery(id+"F0.imprint","IMPRINT",EDGE,{"disambiguationData":[TD([[subQ2,-1.0]])],"derivedFrom":subQ1}),-1.0]])]});}
            var Q60;
            {var subQ0=sQuery(id+"F0.wireOp",EDGE,"E48.5");var subQ1=sQuery(id+"F0.wireOp",EDGE,"E25.3");var subQ2=makeQuery(id+"F0.imprint","INTERSECT",VERTEX,{"derivedFrom":[subQ1,subQ0]});Q60=makeQuery(id+"F0.imprint","IMPRINT",FACE,{"disambiguationData":[TD([[makeQuery(id+"F0.imprint","IMPRINT",EDGE,{"disambiguationData":[TD([[subQ2,-1.0]])],"derivedFrom":subQ1}),-1.0]])]});}
            var Q61;
            {var subQ5=sQuery(id+"F0.wireOp",EDGE,"E25.4");var subQ6=sQuery(id+"F0.wireOp",EDGE,"E25.3");var subQ7=makeQuery(id+"F0.imprint","INTERSECT",VERTEX,{"derivedFrom":[subQ6,subQ5]});Q61=makeQuery(id+"F0.imprint","IMPRINT",FACE,{"disambiguationData":[TD([[makeQuery(id+"F0.imprint","IMPRINT",EDGE,{"disambiguationData":[TD([[subQ7,1.0]])],"derivedFrom":subQ6}),-1.0]])]});}
            var Q62;
            {var subQ0=sQuery(id+"F0.wireOp",EDGE,"0c9a6bff-b2c0-4d4d-a447-967ebe58276c.1");var subQ1=sQuery(id+"F0.wireOp",EDGE,"E25.3");var subQ2=makeQuery(id+"F0.imprint","INTERSECT",VERTEX,{"derivedFrom":[subQ1,subQ0]});Q62=makeQuery(id+"F0.imprint","IMPRINT",FACE,{"disambiguationData":[TD([[makeQuery(id+"F0.imprint","IMPRINT",EDGE,{"disambiguationData":[TD([[subQ2,-1.0]])],"derivedFrom":subQ1}),-1.0]])]});}
            var Q63;
            {var subQ0=sQuery(id+"F0.wireOp",EDGE,"E49.2");var subQ1=sQuery(id+"F0.wireOp",EDGE,"E26.0");var subQ2=makeQuery(id+"F0.imprint","INTERSECT",VERTEX,{"derivedFrom":[subQ1,subQ0]});Q63=makeQuery(id+"F0.imprint","IMPRINT",FACE,{"disambiguationData":[TD([[makeQuery(id+"F0.imprint","IMPRINT",EDGE,{"disambiguationData":[TD([[subQ2,-1.0]])],"derivedFrom":subQ1}),1.0]])]});}
            var Q64;
            {var subQ0=sQuery(id+"F0.wireOp",EDGE,"fe7c7291-770d-4a74-9fde-94e01091e8e7.4");var subQ1=sQuery(id+"F0.wireOp",EDGE,"E25.3");var subQ2=makeQuery(id+"F0.imprint","INTERSECT",VERTEX,{"derivedFrom":[subQ1,subQ0]});Q64=makeQuery(id+"F0.imprint","IMPRINT",FACE,{"disambiguationData":[TD([[makeQuery(id+"F0.imprint","IMPRINT",EDGE,{"disambiguationData":[TD([[subQ2,-1.0]])],"derivedFrom":subQ1}),-1.0]])]});}
            var Q65;
            {var subQ0=sQuery(id+"F0.wireOp",EDGE,"E49.2");var subQ1=sQuery(id+"F0.wireOp",EDGE,"E33.trimOffspring");var subQ2=makeQuery(id+"F0.imprint","INTERSECT",VERTEX,{"derivedFrom":[subQ1,subQ0]});Q65=makeQuery(id+"F0.imprint","IMPRINT",FACE,{"disambiguationData":[TD([[makeQuery(id+"F0.imprint","IMPRINT",EDGE,{"disambiguationData":[TD([[subQ2,-1.0]])],"derivedFrom":subQ1}),1.0]])]});}
            var Q66;
            {var subQ3=sQuery(id+"F0.wireOp",EDGE,"E25.3");var subQ13=sQuery(id+"F0.wireOp",EDGE,"E49.2");var subQ14=makeQuery(id+"F0.imprint","INTERSECT",VERTEX,{"derivedFrom":[subQ3,subQ13]});Q66=makeQuery(id+"F0.imprint","IMPRINT",FACE,{"disambiguationData":[TD([[makeQuery(id+"F0.imprint","IMPRINT",EDGE,{"disambiguationData":[TD([[subQ14,-1.0]])],"derivedFrom":subQ3}),1.0]])]});}
            var Q67;
            {var subQ0=sQuery(id+"F0.wireOp",EDGE,"E61.3");var subQ1=sQuery(id+"F0.wireOp",EDGE,"E20.trimOffspring");var subQ2=makeQuery(id+"F0.imprint","INTERSECT",VERTEX,{"derivedFrom":[subQ1,subQ0]});Q67=makeQuery(id+"F0.imprint","IMPRINT",FACE,{"disambiguationData":[TD([[makeQuery(id+"F0.imprint","IMPRINT",EDGE,{"disambiguationData":[TD([[subQ2,-1.0]])],"derivedFrom":subQ1}),-1.0]])]});}
            var Q68;
            {var subQ0=sQuery(id+"F0.wireOp",EDGE,"fe7c7291-770d-4a74-9fde-94e01091e8e7.1");var subQ1=sQuery(id+"F0.wireOp",EDGE,"E14.5");var subQ2=makeQuery(id+"F0.imprint","INTERSECT",VERTEX,{"derivedFrom":[subQ1,subQ0]});Q68=makeQuery(id+"F0.imprint","IMPRINT",FACE,{"disambiguationData":[TD([[makeQuery(id+"F0.imprint","IMPRINT",EDGE,{"disambiguationData":[TD([[subQ2,-1.0]])],"derivedFrom":subQ1}),1.0]])]});}
            var Q69;
            {var subQ1=sQuery(id+"F0.wireOp",EDGE,"E13.2");var subQ7=sQuery(id+"F0.wireOp",EDGE,"fe7c7291-770d-4a74-9fde-94e01091e8e7.1");var subQ9=makeQuery(id+"F0.imprint","INTERSECT",VERTEX,{"derivedFrom":[subQ1,subQ7]});Q69=makeQuery(id+"F0.imprint","IMPRINT",FACE,{"disambiguationData":[TD([[makeQuery(id+"F0.imprint","IMPRINT",EDGE,{"disambiguationData":[TD([[subQ9,-1.0]])],"derivedFrom":subQ1}),-1.0]])]});}
            var Q70;
            {var subQ1=sQuery(id+"F0.wireOp",EDGE,"E60.0");var subQ12=sQuery(id+"F0.wireOp",EDGE,"E13.2");var subQ13=makeQuery(id+"F0.imprint","INTERSECT",VERTEX,{"derivedFrom":[subQ12,subQ1]});Q70=makeQuery(id+"F0.imprint","IMPRINT",FACE,{"disambiguationData":[TD([[makeQuery(id+"F0.imprint","IMPRINT",EDGE,{"disambiguationData":[TD([[subQ13,-1.0]])],"derivedFrom":subQ12}),1.0]])]});}
            var Q71;
            {var subQ1=sQuery(id+"F0.wireOp",EDGE,"0c9a6bff-b2c0-4d4d-a447-967ebe58276c.3");var subQ7=sQuery(id+"F0.wireOp",EDGE,"E64.0");var subQ8=makeQuery(id+"F0.imprint","INTERSECT",VERTEX,{"derivedFrom":[subQ7,subQ1]});Q71=makeQuery(id+"F0.imprint","IMPRINT",FACE,{"disambiguationData":[TD([[makeQuery(id+"F0.imprint","IMPRINT",EDGE,{"disambiguationData":[TD([[subQ8,-1.0]])],"derivedFrom":subQ7}),1.0]])]});}
            var Q72;
            {var subQ0=sQuery(id+"F0.wireOp",EDGE,"0c9a6bff-b2c0-4d4d-a447-967ebe58276c.3");var subQ1=sQuery(id+"F0.wireOp",EDGE,"E37.5");var subQ2=makeQuery(id+"F0.imprint","INTERSECT",VERTEX,{"derivedFrom":[subQ1,subQ0]});Q72=makeQuery(id+"F0.imprint","IMPRINT",FACE,{"disambiguationData":[TD([[makeQuery(id+"F0.imprint","IMPRINT",EDGE,{"disambiguationData":[TD([[subQ2,-1.0]])],"derivedFrom":subQ1}),-1.0]])]});}
            var Q73;
            {var subQ0=sQuery(id+"F0.wireOp",EDGE,"fe7c7291-770d-4a74-9fde-94e01091e8e7.0");var subQ1=sQuery(id+"F0.wireOp",EDGE,"E37.5");var subQ2=makeQuery(id+"F0.imprint","INTERSECT",VERTEX,{"derivedFrom":[subQ1,subQ0]});Q73=makeQuery(id+"F0.imprint","IMPRINT",FACE,{"disambiguationData":[TD([[makeQuery(id+"F0.imprint","IMPRINT",EDGE,{"disambiguationData":[TD([[subQ2,-1.0]])],"derivedFrom":subQ1}),-1.0]])]});}
            var Q74;
            {var subQ0=sQuery(id+"F0.wireOp",EDGE,"E61.4");var subQ1=sQuery(id+"F0.wireOp",EDGE,"E38.2");var subQ2=makeQuery(id+"F0.imprint","INTERSECT",VERTEX,{"derivedFrom":[subQ1,subQ0]});Q74=makeQuery(id+"F0.imprint","IMPRINT",FACE,{"disambiguationData":[TD([[makeQuery(id+"F0.imprint","IMPRINT",EDGE,{"disambiguationData":[TD([[subQ2,-1.0]])],"derivedFrom":subQ1}),1.0]])]});}
            var Q75;
            {var subQ0=sQuery(id+"F0.wireOp",EDGE,"E60.1");var subQ1=sQuery(id+"F0.wireOp",EDGE,"E37.5");var subQ2=makeQuery(id+"F0.imprint","INTERSECT",VERTEX,{"derivedFrom":[subQ1,subQ0]});Q75=makeQuery(id+"F0.imprint","IMPRINT",FACE,{"disambiguationData":[TD([[makeQuery(id+"F0.imprint","IMPRINT",EDGE,{"disambiguationData":[TD([[subQ2,-1.0]])],"derivedFrom":subQ1}),-1.0]])]});}
            var Q76;
            {var subQ0=sQuery(id+"F0.wireOp",EDGE,"0ac59062-be46-4c43-8f9f-82bc203d06fa.trimOffspring");var subQ1=sQuery(id+"F0.wireOp",EDGE,"E37.0");var subQ2=makeQuery(id+"F0.imprint","INTERSECT",VERTEX,{"derivedFrom":[subQ1,subQ0]});Q76=makeQuery(id+"F0.imprint","IMPRINT",FACE,{"disambiguationData":[TD([[makeQuery(id+"F0.imprint","IMPRINT",EDGE,{"disambiguationData":[TD([[subQ2,-1.0]])],"derivedFrom":subQ1}),-1.0]])]});}
            var Q77;
            {var subQ0=sQuery(id+"F0.wireOp",EDGE,"E48.4");var subQ1=sQuery(id+"F0.wireOp",EDGE,"E42.0");var subQ2=makeQuery(id+"F0.imprint","INTERSECT",VERTEX,{"derivedFrom":[subQ1,subQ0]});Q77=makeQuery(id+"F0.imprint","IMPRINT",FACE,{"disambiguationData":[TD([[makeQuery(id+"F0.imprint","IMPRINT",EDGE,{"disambiguationData":[TD([[subQ2,-1.0]])],"derivedFrom":subQ1}),1.0]])]});}
            var Q78;
            {var subQ1=sQuery(id+"F0.wireOp",EDGE,"0c9a6bff-b2c0-4d4d-a447-967ebe58276c.1");var subQ3=sQuery(id+"F0.wireOp",EDGE,"E50.0");var subQ4=makeQuery(id+"F0.imprint","INTERSECT",VERTEX,{"derivedFrom":[subQ3,subQ1]});Q78=makeQuery(id+"F0.imprint","IMPRINT",FACE,{"disambiguationData":[TD([[makeQuery(id+"F0.imprint","IMPRINT",EDGE,{"disambiguationData":[TD([[subQ4,-1.0]])],"derivedFrom":subQ3}),1.0]])]});}
            var Q79;
            {var subQ0=sQuery(id+"F0.wireOp",EDGE,"E49.1");var subQ1=sQuery(id+"F0.wireOp",EDGE,"E37.0");var subQ2=makeQuery(id+"F0.imprint","INTERSECT",VERTEX,{"derivedFrom":[subQ1,subQ0]});Q79=makeQuery(id+"F0.imprint","IMPRINT",FACE,{"disambiguationData":[TD([[makeQuery(id+"F0.imprint","IMPRINT",EDGE,{"disambiguationData":[TD([[subQ2,-1.0]])],"derivedFrom":subQ1}),-1.0]])]});}
            var Q80;
            {var subQ0=sQuery(id+"F0.wireOp",EDGE,"fe7c7291-770d-4a74-9fde-94e01091e8e7.5");var subQ1=sQuery(id+"F0.wireOp",EDGE,"E38.3");var subQ2=makeQuery(id+"F0.imprint","INTERSECT",VERTEX,{"derivedFrom":[subQ1,subQ0]});Q80=makeQuery(id+"F0.imprint","IMPRINT",FACE,{"disambiguationData":[TD([[makeQuery(id+"F0.imprint","IMPRINT",EDGE,{"disambiguationData":[TD([[subQ2,-1.0]])],"derivedFrom":subQ1}),1.0]])]});}
            var Q81;
            {var subQ1=sQuery(id+"F0.wireOp",EDGE,"E37.0");var subQ7=sQuery(id+"F0.wireOp",EDGE,"fe7c7291-770d-4a74-9fde-94e01091e8e7.5");var subQ9=makeQuery(id+"F0.imprint","INTERSECT",VERTEX,{"derivedFrom":[subQ1,subQ7]});Q81=makeQuery(id+"F0.imprint","IMPRINT",FACE,{"disambiguationData":[TD([[makeQuery(id+"F0.imprint","IMPRINT",EDGE,{"disambiguationData":[TD([[subQ9,-1.0]])],"derivedFrom":subQ1}),-1.0]])]});}
            var Q82;
            {var subQ3=sQuery(id+"F0.wireOp",EDGE,"E1.3");var subQ6=sQuery(id+"F0.wireOp",EDGE,"E13.1");var subQ10=makeQuery(id+"F0.imprint","INTERSECT",VERTEX,{"derivedFrom":[subQ3,subQ6]});Q82=makeQuery(id+"F0.imprint","IMPRINT",FACE,{"disambiguationData":[TD([[makeQuery(id+"F0.imprint","IMPRINT",EDGE,{"disambiguationData":[TD([[subQ10,-1.0]])],"derivedFrom":subQ3}),1.0]])]});}
            var Q83;
            {var subQ0=sQuery(id+"F0.wireOp",EDGE,"E26.1");var subQ9=sQuery(id+"F0.wireOp",EDGE,"E1.2");var subQ11=makeQuery(id+"F0.imprint","INTERSECT",VERTEX,{"derivedFrom":[subQ9,subQ0]});Q83=makeQuery(id+"F0.imprint","IMPRINT",FACE,{"disambiguationData":[TD([[makeQuery(id+"F0.imprint","IMPRINT",EDGE,{"disambiguationData":[TD([[subQ11,-1.0]])],"derivedFrom":subQ9}),1.0]])]});}
            extrude(context, id + "F1", {"entities" : qUnion([Q0, Q1, Q2, Q3, Q4, Q5, Q6, Q7, Q8, Q9, Q10, Q11, Q12, Q13, Q14, Q15, Q16, Q17, Q18, Q19, Q20, Q21, Q22, Q23, Q24, Q25, Q26, Q27, Q28, Q29, Q30, Q31, Q32, Q33, Q34, Q35, Q36, Q37, Q38, Q39, Q40, Q41, Q42, Q43, Q44, Q45, Q46, Q47, Q48, Q49, Q50, Q51, Q52, Q53, Q54, Q55, Q56, Q57, Q58, Q59, Q60, Q61, Q62, Q63, Q64, Q65, Q66, Q67, Q68, Q69, Q70, Q71, Q72, Q73, Q74, Q75, Q76, Q77, Q78, Q79, Q80, Q81, Q82, Q83]), "depth" : 2 * mm, "offsetDistance" : 25 * mm});
        }
    });
